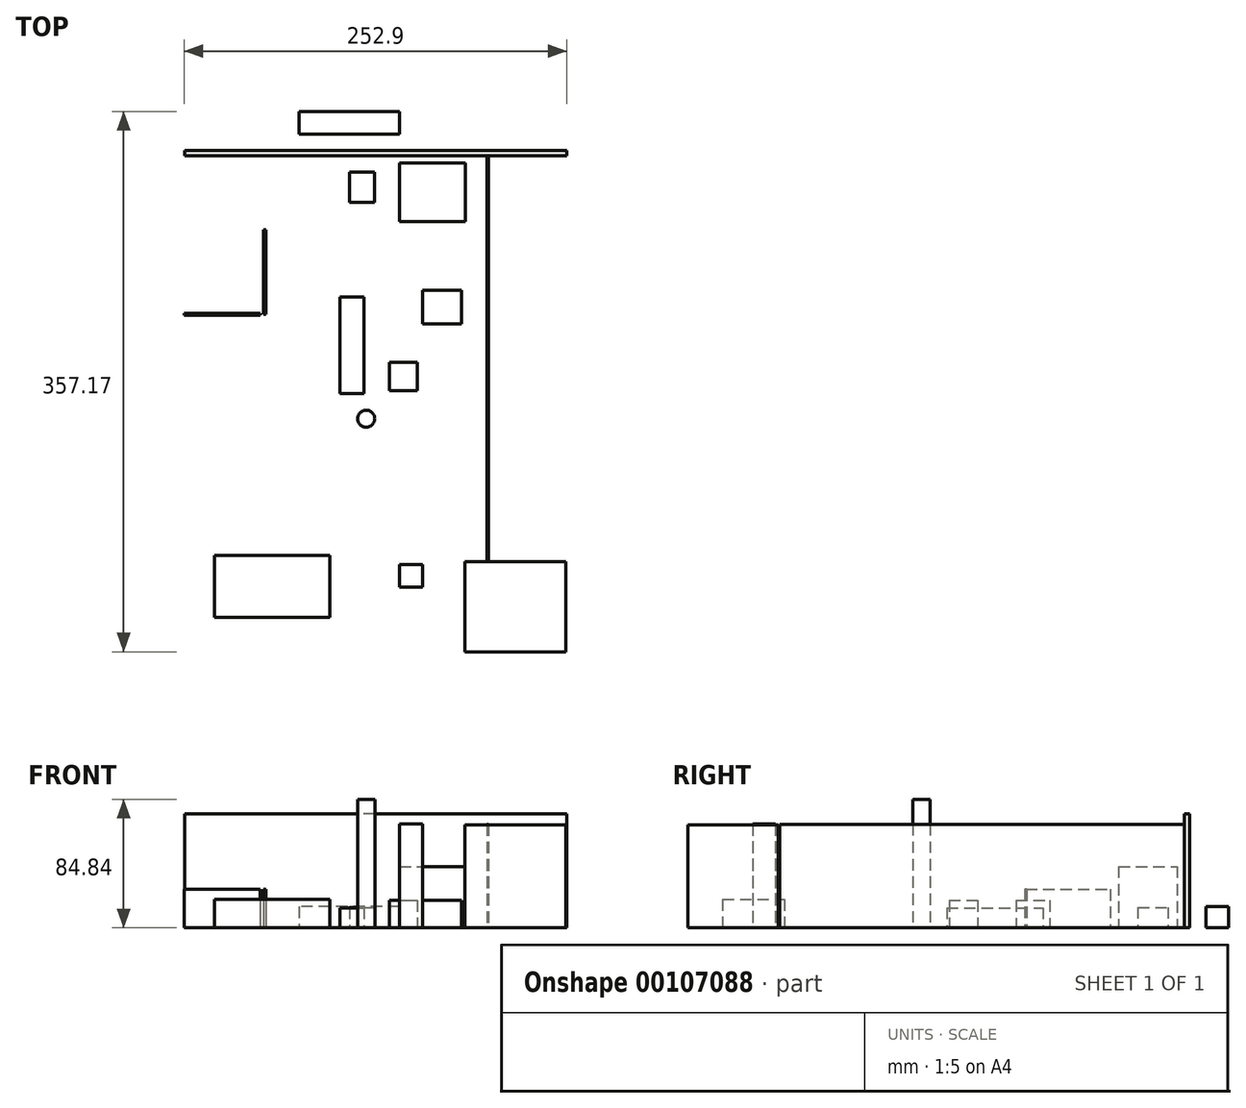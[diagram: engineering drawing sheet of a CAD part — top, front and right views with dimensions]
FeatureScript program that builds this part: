
annotation { "Feature Type Name" : "Feature", "Feature Type Description" : "" }
export const myFeature = defineFeature(function(context is Context, id is Id, definition is map)
    precondition{}
    {
        {
            var Q0;
            Q0=qCreatedBy(makeId("Top.planeOp"),FACE);
            var sketch = newSketch(context, id + "F0", { "sketchPlane" : qUnion([Q0])});
            skLineSegment(sketch, "E0.bottom", {"start": v(43.07, -214.58) * mm, "end": v(108.25, -214.58) * mm});
            skLineSegment(sketch, "E0.top", {"start": v(43.07, -159.08) * mm, "end": v(108.25, -159.08) * mm});
            skLineSegment(sketch, "E0.left", {"start": v(43.07, -214.58) * mm, "end": v(43.07, -159.08) * mm});
            skLineSegment(sketch, "E0.right", {"start": v(108.25, -214.58) * mm, "end": v(108.25, -159.08) * mm});
            skLineSegment(sketch, "E1.bottom", {"start": v(43.07, -159.08) * mm, "end": v(0, -159.08) * mm});
            skLineSegment(sketch, "E1.top", {"start": v(43.07, -217.37) * mm, "end": v(0, -217.37) * mm});
            skLineSegment(sketch, "E1.left", {"start": v(43.07, -159.08) * mm, "end": v(43.07, -217.37) * mm});
            skLineSegment(sketch, "E1.right", {"start": v(0, -159.08) * mm, "end": v(0, -217.37) * mm});
            skLineSegment(sketch, "E2.bottom", {"start": v(0, -159.08) * mm, "end": v(15.02, -159.08) * mm});
            skLineSegment(sketch, "E2.top", {"start": v(0, -173.94) * mm, "end": v(15.02, -173.94) * mm});
            skLineSegment(sketch, "E2.left", {"start": v(0, -159.08) * mm, "end": v(0, -173.94) * mm});
            skLineSegment(sketch, "E2.right", {"start": v(15.02, -159.08) * mm, "end": v(15.02, -173.94) * mm});
            skSolve(sketch);
        }
        {
            var Q0;
            {var subQ3=sQuery(id+"F0.wireOp",EDGE,"E1.bottom");Q0=makeQuery(id+"F0.imprint","IMPRINT",FACE,{"disambiguationData":[TD([[makeQuery(id+"F0.imprint","IMPRINT",EDGE,{"derivedFrom":subQ3}),1.0]])]});}
            extrude(context, id + "F1", {"entities" : qUnion([Q0]), "depth" : 68.77 * mm});
        }
        {
            var Q0;
            Q0=qCreatedBy(makeId("Top.planeOp"),FACE);
            var sketch = newSketch(context, id + "F2", { "sketchPlane" : qUnion([Q0])});
            skLineSegment(sketch, "E3.bottom", {"start": v(43.14, -216.7) * mm, "end": v(109.8, -216.7) * mm});
            skLineSegment(sketch, "E3.top", {"start": v(43.14, -157.03) * mm, "end": v(109.8, -157.03) * mm});
            skLineSegment(sketch, "E3.left", {"start": v(43.14, -216.7) * mm, "end": v(43.14, -157.03) * mm});
            skLineSegment(sketch, "E3.right", {"start": v(109.8, -216.7) * mm, "end": v(109.8, -157.03) * mm});
            skSolve(sketch);
        }
        {
            var Q0;
            Q0=makeQuery(id+"F2.imprint","IMPRINT",FACE,{"disambiguationData":[TD([[makeQuery(id+"F2.imprint","IMPRINT",EDGE,{"derivedFrom":sQuery(id+"F2.wireOp",EDGE,"E3.bottom")}),1.0]])]});
            extrude(context, id + "F3", {"entities" : qUnion([Q0]), "depth" : 68.1 * mm});
        }
        {
            var Q0;
            Q0=qCreatedBy(makeId("Top.planeOp"),FACE);
            var sketch = newSketch(context, id + "F4", { "sketchPlane" : qUnion([Q0])});
            skLineSegment(sketch, "E4.bottom", {"start": v(-122.21, -193.82) * mm, "end": v(-46.06, -193.82) * mm});
            skLineSegment(sketch, "E4.top", {"start": v(-122.21, -153.02) * mm, "end": v(-46.06, -153.02) * mm});
            skLineSegment(sketch, "E4.left", {"start": v(-122.21, -193.82) * mm, "end": v(-122.21, -153.02) * mm});
            skLineSegment(sketch, "E4.right", {"start": v(-46.06, -193.82) * mm, "end": v(-46.06, -153.02) * mm});
            skSolve(sketch);
        }
        {
            var Q0;
            Q0 = qSketchRegion(id + "F4", true);
            extrude(context, id + "F5", {"entities" : qUnion([Q0]), "depth" : 18.72 * mm});
        }
        {
            var Q0;
            Q0=qCreatedBy(makeId("Top.planeOp"),FACE);
            var sketch = newSketch(context, id + "F6", { "sketchPlane" : qUnion([Q0])});
            skLineSegment(sketch, "E5.bottom", {"start": v(-39.53, -45.82) * mm, "end": v(-23.64, -45.82) * mm});
            skLineSegment(sketch, "E5.top", {"start": v(-39.53, 17.9) * mm, "end": v(-23.64, 17.9) * mm});
            skLineSegment(sketch, "E5.left", {"start": v(-39.53, -45.82) * mm, "end": v(-39.53, 17.9) * mm});
            skLineSegment(sketch, "E5.right", {"start": v(-23.64, -45.82) * mm, "end": v(-23.64, 17.9) * mm});
            skSolve(sketch);
        }
        {
            var Q0;
            Q0=makeQuery(id+"F6.imprint","IMPRINT",FACE,{"disambiguationData":[TD([[makeQuery(id+"F6.imprint","IMPRINT",EDGE,{"derivedFrom":sQuery(id+"F6.wireOp",EDGE,"E5.bottom")}),1.0]])]});
            extrude(context, id + "F7", {"entities" : qUnion([Q0]), "depth" : 13.16 * mm});
        }
        {
            var Q0;
            Q0=qCreatedBy(makeId("Top.planeOp"),FACE);
            var sketch = newSketch(context, id + "F8", { "sketchPlane" : qUnion([Q0])});
            skLineSegment(sketch, "E6.bottom", {"start": v(-6.73, -44.18) * mm, "end": v(11.68, -44.18) * mm});
            skLineSegment(sketch, "E6.top", {"start": v(-6.73, -25.28) * mm, "end": v(11.68, -25.28) * mm});
            skLineSegment(sketch, "E6.left", {"start": v(-6.73, -44.18) * mm, "end": v(-6.73, -25.28) * mm});
            skLineSegment(sketch, "E6.right", {"start": v(11.68, -44.18) * mm, "end": v(11.68, -25.28) * mm});
            skSolve(sketch);
        }
        {
            var Q0;
            Q0 = qSketchRegion(id + "F8", true);
            extrude(context, id + "F9", {"entities" : qUnion([Q0]), "depth" : 18.06 * mm});
        }
        {
            var Q0;
            Q0=qCreatedBy(makeId("Top.planeOp"),FACE);
            var sketch = newSketch(context, id + "F10", { "sketchPlane" : qUnion([Q0])});
            skLineSegment(sketch, "E7.bottom", {"start": v(0, 67.68) * mm, "end": v(43.35, 67.68) * mm});
            skLineSegment(sketch, "E7.top", {"start": v(0, 106.37) * mm, "end": v(43.35, 106.37) * mm});
            skLineSegment(sketch, "E7.left", {"start": v(0, 67.68) * mm, "end": v(0, 106.37) * mm});
            skLineSegment(sketch, "E7.right", {"start": v(43.35, 67.68) * mm, "end": v(43.35, 106.37) * mm});
            skSolve(sketch);
        }
        {
            var Q0;
            Q0 = qSketchRegion(id + "F10", true);
            extrude(context, id + "F11", {"entities" : qUnion([Q0]), "depth" : 40.4 * mm});
        }
        {
            var Q0;
            Q0=qCreatedBy(makeId("Top.planeOp"),FACE);
            var sketch = newSketch(context, id + "F12", { "sketchPlane" : qUnion([Q0])});
            skLineSegment(sketch, "E8.bottom", {"start": v(-32.96, 80.51) * mm, "end": v(-16.5, 80.51) * mm});
            skLineSegment(sketch, "E8.top", {"start": v(-32.96, 100.28) * mm, "end": v(-16.5, 100.28) * mm});
            skLineSegment(sketch, "E8.left", {"start": v(-32.96, 80.51) * mm, "end": v(-32.96, 100.28) * mm});
            skLineSegment(sketch, "E8.right", {"start": v(-16.5, 80.51) * mm, "end": v(-16.5, 100.28) * mm});
            skSolve(sketch);
        }
        {
            var Q0;
            Q0 = qSketchRegion(id + "F12", true);
            extrude(context, id + "F13", {"entities" : qUnion([Q0]), "depth" : 13.53 * mm});
        }
        {
            var Q0;
            Q0=qCreatedBy(makeId("Top.planeOp"),FACE);
            var sketch = newSketch(context, id + "F14", { "sketchPlane" : qUnion([Q0])});
            skLineSegment(sketch, "E9.bottom", {"start": v(0, 125.5) * mm, "end": v(-66.45, 125.5) * mm});
            skLineSegment(sketch, "E9.top", {"start": v(0, 140.46) * mm, "end": v(-66.45, 140.46) * mm});
            skLineSegment(sketch, "E9.left", {"start": v(0, 125.5) * mm, "end": v(0, 140.46) * mm});
            skLineSegment(sketch, "E9.right", {"start": v(-66.45, 125.5) * mm, "end": v(-66.45, 140.46) * mm});
            skSolve(sketch);
        }
        {
            var Q0;
            Q0 = qSketchRegion(id + "F14", true);
            extrude(context, id + "F15", {"entities" : qUnion([Q0]), "depth" : 14.05 * mm});
        }
        {
            var Q0;
            Q0=qCreatedBy(makeId("Top.planeOp"),FACE);
            var sketch = newSketch(context, id + "F16", { "sketchPlane" : qUnion([Q0])});
            skLineSegment(sketch, "E10.bottom", {"start": v(40.75, 0) * mm, "end": v(15.26, 0) * mm});
            skLineSegment(sketch, "E10.top", {"start": v(40.75, 22.34) * mm, "end": v(15.26, 22.34) * mm});
            skLineSegment(sketch, "E10.left", {"start": v(40.75, 0) * mm, "end": v(40.75, 22.34) * mm});
            skLineSegment(sketch, "E10.right", {"start": v(15.26, 0) * mm, "end": v(15.26, 22.34) * mm});
            skSolve(sketch);
        }
        {
            var Q0;
            Q0 = qSketchRegion(id + "F16", true);
            extrude(context, id + "F17", {"entities" : qUnion([Q0]), "depth" : 18.03 * mm});
        }
        {
            var Q0;
            Q0=qCreatedBy(makeId("Top.planeOp"),FACE);
            var sketch = newSketch(context, id + "F18", { "sketchPlane" : qUnion([Q0])});
            skLineSegment(sketch, "E11.bottom", {"start": v(-142.4, 6.95) * mm, "end": v(-92.2, 6.95) * mm});
            skLineSegment(sketch, "E11.top", {"start": v(-142.4, 5.76) * mm, "end": v(-92.2, 5.76) * mm});
            skLineSegment(sketch, "E11.left", {"start": v(-142.4, 6.95) * mm, "end": v(-142.4, 5.76) * mm});
            skLineSegment(sketch, "E11.right", {"start": v(-92.2, 6.95) * mm, "end": v(-92.2, 5.76) * mm});
            skSolve(sketch);
        }
        {
            var Q0;
            Q0 = qSketchRegion(id + "F18", true);
            extrude(context, id + "F19", {"entities" : qUnion([Q0]), "depth" : 25.4 * mm});
        }
        {
            var Q0;
            Q0=qCreatedBy(makeId("Top.planeOp"),FACE);
            var sketch = newSketch(context, id + "F20", { "sketchPlane" : qUnion([Q0])});
            skLineSegment(sketch, "E12.bottom", {"start": v(-88.34, 6.44) * mm, "end": v(-90.04, 6.44) * mm});
            skLineSegment(sketch, "E12.top", {"start": v(-88.34, 62.26) * mm, "end": v(-90.04, 62.26) * mm});
            skLineSegment(sketch, "E12.left", {"start": v(-88.34, 6.44) * mm, "end": v(-88.34, 62.26) * mm});
            skLineSegment(sketch, "E12.right", {"start": v(-90.04, 6.44) * mm, "end": v(-90.04, 62.26) * mm});
            skSolve(sketch);
        }
        {
            var Q0;
            Q0 = qSketchRegion(id + "F20", true);
            extrude(context, id + "F21", {"entities" : qUnion([Q0]), "depth" : 25.4 * mm});
        }
        {
            var Q0;
            Q0=qCreatedBy(makeId("Top.planeOp"),FACE);
            var sketch = newSketch(context, id + "F22", { "sketchPlane" : qUnion([Q0])});
            skLineSegment(sketch, "E13.bottom", {"start": v(110.5, 114.67) * mm, "end": v(-142.06, 114.67) * mm});
            skLineSegment(sketch, "E13.top", {"start": v(110.5, 111.23) * mm, "end": v(-142.06, 111.23) * mm});
            skLineSegment(sketch, "E13.left", {"start": v(110.5, 114.67) * mm, "end": v(110.5, 111.23) * mm});
            skLineSegment(sketch, "E13.right", {"start": v(-142.06, 114.67) * mm, "end": v(-142.06, 111.23) * mm});
            skSolve(sketch);
        }
        {
            var Q0;
            Q0 = qSketchRegion(id + "F22", true);
            extrude(context, id + "F23", {"entities" : qUnion([Q0]), "depth" : 75.28 * mm});
        }
        {
            var Q0;
            Q0=makeQuery(id+"F23.opExtrude","SWEPT_FACE",FACE,{"disambiguationData":[OSD([sQuery(id+"F22.wireOp",EDGE,"E13.bottom")])]});
            var sketch = newSketch(context, id + "F24", { "sketchPlane" : qUnion([Q0])});
            skSolve(sketch);
        }
        {
            var Q0;
            Q0=qCreatedBy(makeId("Top.planeOp"),FACE);
            var sketch = newSketch(context, id + "F25", { "sketchPlane" : qUnion([Q0])});
            skLineSegment(sketch, "E14.bottom", {"start": v(57.74, -156.24) * mm, "end": v(58.77, -156.24) * mm});
            skLineSegment(sketch, "E14.top", {"start": v(57.74, 112.3) * mm, "end": v(58.77, 112.3) * mm});
            skLineSegment(sketch, "E14.left", {"start": v(57.74, -156.24) * mm, "end": v(57.74, 112.3) * mm});
            skLineSegment(sketch, "E14.right", {"start": v(58.77, -156.24) * mm, "end": v(58.77, 112.3) * mm});
            skSolve(sketch);
        }
        {
            var Q0;
            Q0 = qSketchRegion(id + "F25", true);
            extrude(context, id + "F26", {"entities" : qUnion([Q0]), "operationType" : NewBodyOperationType.ADD, "depth" : 68.44 * mm});
        }
        {
            var Q0;
            Q0=qCreatedBy(makeId("Top.planeOp"),FACE);
            var sketch = newSketch(context, id + "F27", { "sketchPlane" : qUnion([Q0])});
            skCircle(sketch, "E15", {"center": v(-22.06, -62.56) * mm, "radius": 5.64 * mm});
            skSolve(sketch);
        }
        {
            var Q0;
            Q0 = qSketchRegion(id + "F27", true);
            extrude(context, id + "F28", {"entities" : qUnion([Q0]), "depth" : 84.84 * mm});
        }
    });
